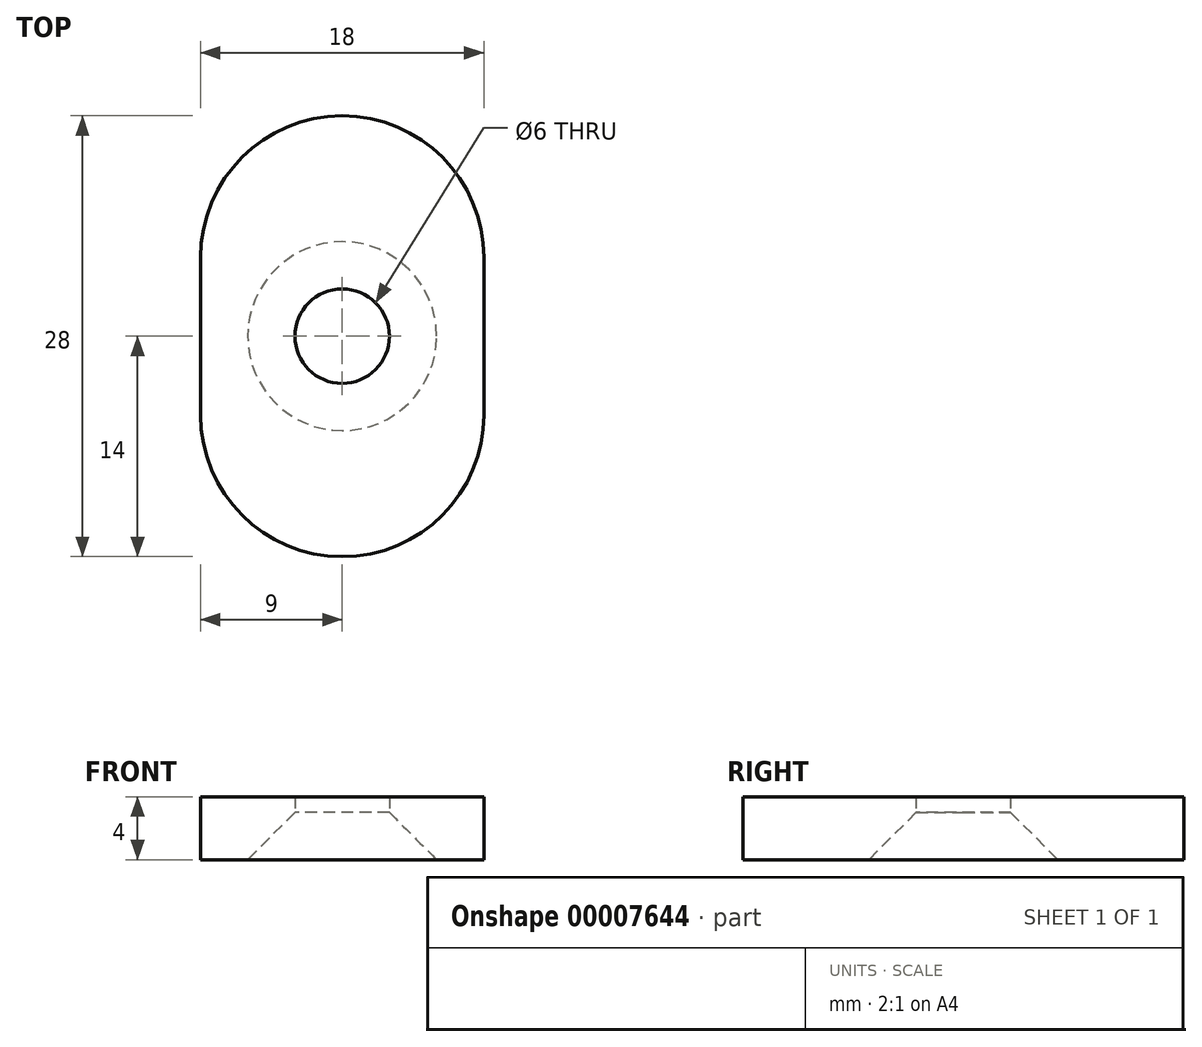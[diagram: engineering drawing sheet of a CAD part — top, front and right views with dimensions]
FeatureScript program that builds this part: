
annotation { "Feature Type Name" : "Feature", "Feature Type Description" : "" }
export const myFeature = defineFeature(function(context is Context, id is Id, definition is map)
    precondition{}
    {
        {
            var Q0;
            Q0=qCreatedBy(makeId("Top.planeOp"),FACE);
            var sketch = newSketch(context, id + "F0", { "sketchPlane" : qUnion([Q0])});
            skCircle(sketch, "E0", {"center": v(0, 0) * mm, "radius": 3 * mm});
            skLineSegment(sketch, "E1", {"start": v(-9, -5) * mm, "end": v(-9, 5) * mm});
            skArc(sketch, "E2", {"start": v(-9, 5) * mm, "mid": v(0, 14) * mm, "end": v(9, 5) * mm});
            skLineSegment(sketch, "E3", {"start": v(9, 5) * mm, "end": v(9, -5) * mm});
            skArc(sketch, "E4", {"start": v(9, -5) * mm, "mid": v(0, -14) * mm, "end": v(-9, -5) * mm});
            skLineSegment(sketch, "E5", {"start": v(0, 5) * mm, "end": v(0, -5) * mm, "construction": true});
            skSolve(sketch);
        }
        {
            var Q0;
            Q0 = qSketchRegion(id + "F0", true);
            extrude(context, id + "F1", {"entities" : qUnion([Q0]), "depth" : 4 * mm, "symmetric" : true});
        }
        {
            var Q0;
            Q0=makeQuery(id+"F1.opExtrude","CAP_EDGE",EDGE,{"disambiguationData":[OSD([sQuery(id+"F0.wireOp",EDGE,"E0")])],"isStart":true});
            chamfer(context, id + "F2", {"entities" : qUnion([Q0]), "chamferType" : ChamferType.OFFSET_ANGLE, "width" : 3 * mm, "oppositeDirection" : false, "angle" : 45 * degree, "tangentPropagation" : true});
        }
    });
